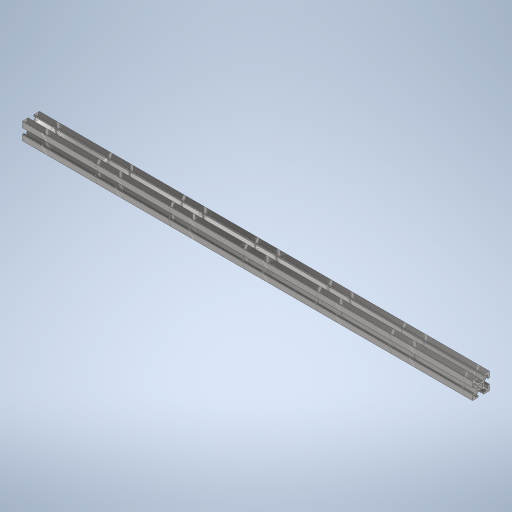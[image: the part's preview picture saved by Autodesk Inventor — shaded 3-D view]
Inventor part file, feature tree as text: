
AUTODESK INVENTOR PART (.ipt)
format: ipt  version: 2023 (Build 270158000, 158)  size: 399,872 bytes
history: native  units: mm
features: extrude x1, sketch x1
ambient origin geometry x8: Origin, YZ Plane, XZ Plane, XY Plane, X Axis, Y Axis, Z Axis, Center Point
bodies: Solide1 (feature_tree)
feature tree (2):
  extrude  "Extrusion1"  Depth=10.0mm
  sketch  "Esquisse1"
